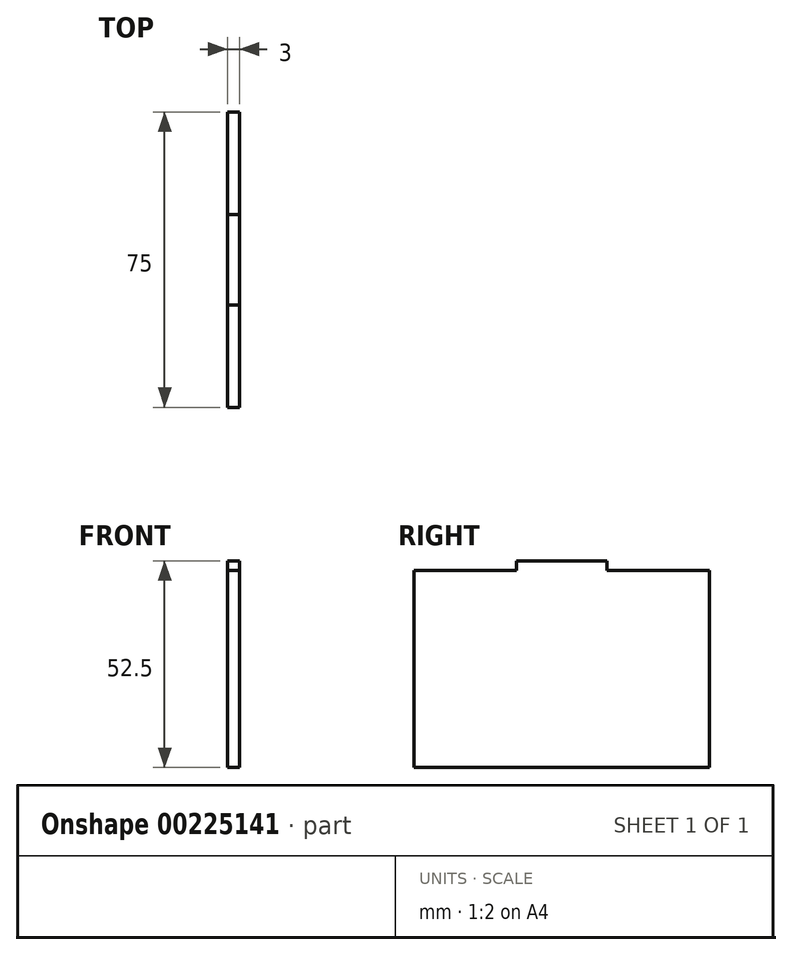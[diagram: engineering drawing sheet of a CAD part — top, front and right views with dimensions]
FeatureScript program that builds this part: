
annotation { "Feature Type Name" : "Feature", "Feature Type Description" : "" }
export const myFeature = defineFeature(function(context is Context, id is Id, definition is map)
    precondition{}
    {
        {
            var Q0;
            Q0=qCreatedBy(makeId("Right.planeOp"),FACE);
            var sketch = newSketch(context, id + "F0", { "sketchPlane" : qUnion([Q0])});
            skLineSegment(sketch, "E0.bottom", {"start": v(-16.7, 28.2) * mm, "end": v(58.3, 28.2) * mm});
            skLineSegment(sketch, "E0.top", {"start": v(-16.7, -21.8) * mm, "end": v(58.3, -21.8) * mm});
            skLineSegment(sketch, "E0.left", {"start": v(-16.7, 28.2) * mm, "end": v(-16.7, -21.8) * mm});
            skLineSegment(sketch, "E0.right", {"start": v(58.3, 28.2) * mm, "end": v(58.3, -21.8) * mm});
            skLineSegment(sketch, "E1.bottom", {"start": v(9.3, 28.2) * mm, "end": v(32.3, 28.2) * mm});
            skLineSegment(sketch, "E1.top", {"start": v(9.3, 30.7) * mm, "end": v(32.3, 30.7) * mm});
            skLineSegment(sketch, "E1.left", {"start": v(9.3, 28.2) * mm, "end": v(9.3, 30.7) * mm});
            skLineSegment(sketch, "E1.right", {"start": v(32.3, 28.2) * mm, "end": v(32.3, 30.7) * mm});
            skLineSegment(sketch, "E2", {"start": v(9.3, 28.2) * mm, "end": v(-16.7, 28.2) * mm});
            skLineSegment(sketch, "E3", {"start": v(32.3, 28.2) * mm, "end": v(58.3, 28.2) * mm});
            skSolve(sketch);
        }
        {
            var Q0;
            Q0 = qSketchRegion(id + "F0", true);
            extrude(context, id + "F1", {"entities" : qUnion([Q0]), "depth" : 3 * mm});
        }
    });
